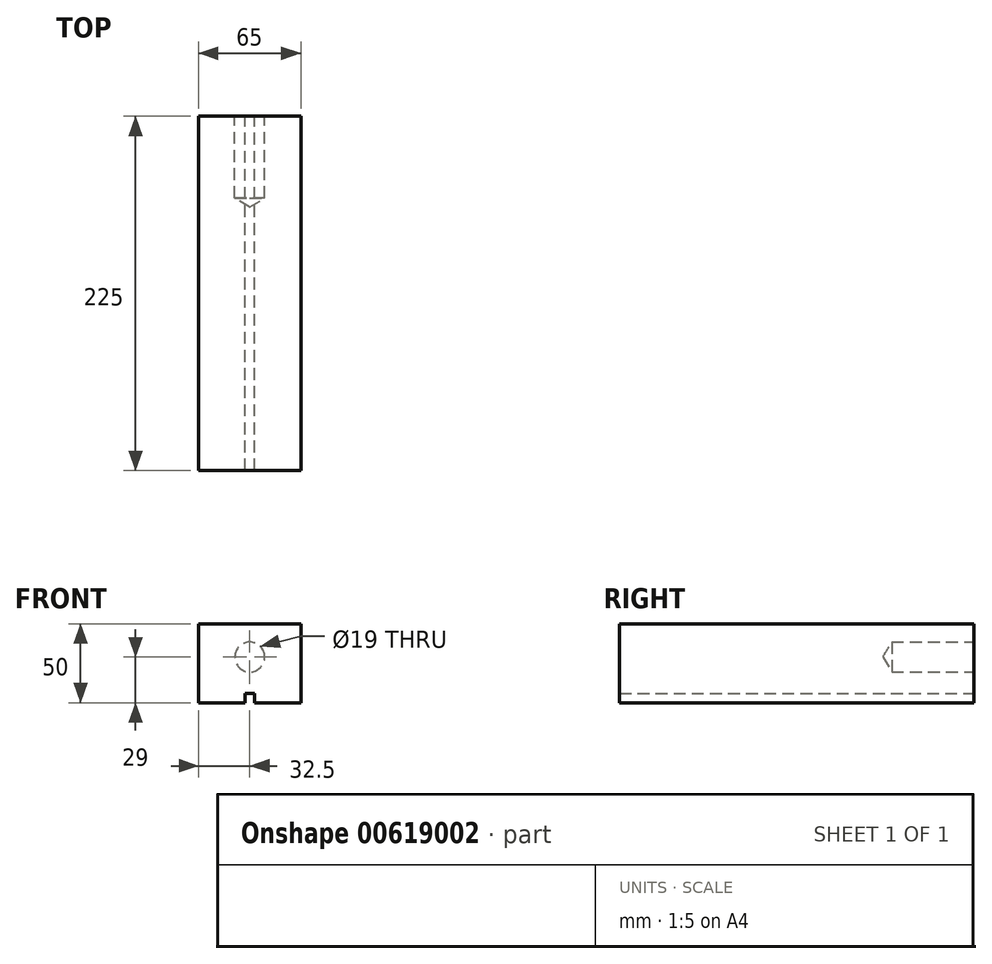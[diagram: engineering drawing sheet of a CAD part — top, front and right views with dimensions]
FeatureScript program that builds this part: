
annotation { "Feature Type Name" : "Feature", "Feature Type Description" : "" }
export const myFeature = defineFeature(function(context is Context, id is Id, definition is map)
    precondition{}
    {
        {
            var Q0;
            Q0=qCreatedBy(makeId("Front.planeOp"),FACE);
            var sketch = newSketch(context, id + "F0", { "sketchPlane" : qUnion([Q0])});
            skLineSegment(sketch, "E0.bottom", {"start": v(0, 21) * mm, "end": v(32.5, 21) * mm});
            skLineSegment(sketch, "E0.top", {"start": v(3, -29) * mm, "end": v(32.5, -29) * mm});
            skLineSegment(sketch, "E0.left", {"start": v(0, 21) * mm, "end": v(0, -23) * mm});
            skLineSegment(sketch, "E0.right", {"start": v(32.5, 21) * mm, "end": v(32.5, -29) * mm});
            skLineSegment(sketch, "E1.top", {"start": v(0, -23) * mm, "end": v(3, -23) * mm});
            skLineSegment(sketch, "E1.right", {"start": v(3, -29) * mm, "end": v(3, -23) * mm});
            skSolve(sketch);
        }
        {
            var Q0;
            Q0 = qSketchRegion(id + "F0", true);
            extrude(context, id + "F1", {"entities" : qUnion([Q0]), "depth" : 225 * mm, "offsetDistance" : 25 * mm});
        }
        {
            var Q0;
            Q0=makeQuery(id+"F1.opExtrude","CAP_FACE",FACE,{"disambiguationData":[OSD([sQuery(id+"F0.wireOp",EDGE,"E0.bottom"),sQuery(id+"F0.wireOp",EDGE,"E0.top"),sQuery(id+"F0.wireOp",EDGE,"E0.left"),sQuery(id+"F0.wireOp",EDGE,"E0.right"),sQuery(id+"F0.wireOp",EDGE,"E1.top"),sQuery(id+"F0.wireOp",EDGE,"E1.right")])],"isStart":true});
            var sketch = newSketch(context, id + "F2", { "sketchPlane" : qUnion([Q0])});
            skPoint(sketch, "E2", {"position": v(0, 0) * mm});
            skSolve(sketch);
        }
        {
            var Q0;
            Q0=sQuery(id+"F2.wireOp",VERTEX,"E2");
            var Q1;
            Q1=makeQuery(id+"F1.opExtrude","SWEPT_BODY",BODY,{"disambiguationData":[OSD([sQuery(id+"F0.wireOp",EDGE,"E0.bottom"),sQuery(id+"F0.wireOp",EDGE,"E0.top"),sQuery(id+"F0.wireOp",EDGE,"E0.left"),sQuery(id+"F0.wireOp",EDGE,"E0.right"),sQuery(id+"F0.wireOp",EDGE,"E1.top"),sQuery(id+"F0.wireOp",EDGE,"E1.right")])]});
            hole(context, id + "F3", {"style" : HoleStyle.SIMPLE, "endStyle" : HoleEndStyle.BLIND, "holeDiameter" : 19 * mm, "majorDiameter" : 5 * mm, "holeDepth" : 52 * mm, "isTappedThrough" : true, "tappedDepth" : 12 * mm, "tapClearance" : 3, "locations" : qUnion([Q0]), "scope" : qUnion([Q1])});
        }
        {
            var Q0;
            Q0=makeQuery(id+"F1.opExtrude","SWEPT_BODY",BODY,{"disambiguationData":[OSD([sQuery(id+"F0.wireOp",EDGE,"E0.bottom"),sQuery(id+"F0.wireOp",EDGE,"E0.top"),sQuery(id+"F0.wireOp",EDGE,"E0.left"),sQuery(id+"F0.wireOp",EDGE,"E0.right"),sQuery(id+"F0.wireOp",EDGE,"E1.top"),sQuery(id+"F0.wireOp",EDGE,"E1.right")])]});
            var Q1;
            Q1=makeQuery(id+"F1.opExtrude","SWEPT_FACE",FACE,{"disambiguationData":[OSD([sQuery(id+"F0.wireOp",EDGE,"E0.left")])]});
            mirror(context, id + "F4", {"operationType" : NewBodyOperationType.ADD, "entities" : qUnion([Q0]), "mirrorPlane" : qUnion([Q1])});
        }
    });
